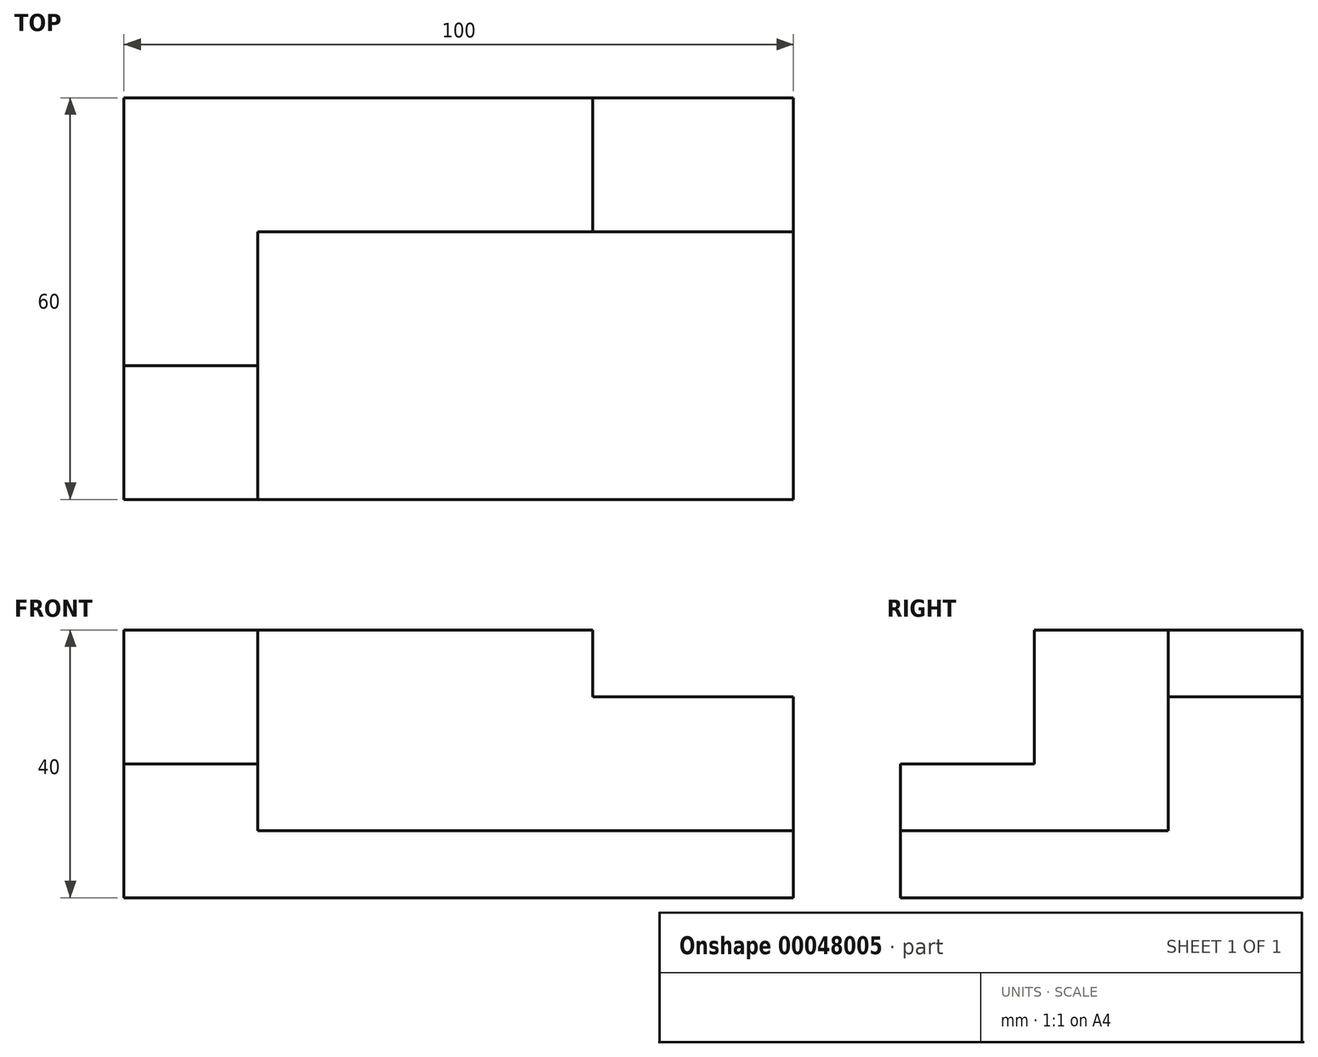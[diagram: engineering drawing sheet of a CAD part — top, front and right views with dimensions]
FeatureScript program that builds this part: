
annotation { "Feature Type Name" : "Feature", "Feature Type Description" : "" }
export const myFeature = defineFeature(function(context is Context, id is Id, definition is map)
    precondition{}
    {
        {
            var Q0;
            Q0=qCreatedBy(makeId("Top.planeOp"),FACE);
            var sketch = newSketch(context, id + "F0", { "sketchPlane" : qUnion([Q0])});
            skLineSegment(sketch, "E0.bottom", {"start": v(0, 0) * mm, "end": v(100, 0) * mm});
            skLineSegment(sketch, "E0.top", {"start": v(0, 60) * mm, "end": v(100, 60) * mm});
            skLineSegment(sketch, "E0.left", {"start": v(0, 0) * mm, "end": v(0, 60) * mm});
            skLineSegment(sketch, "E0.right", {"start": v(100, 0) * mm, "end": v(100, 60) * mm});
            skSolve(sketch);
        }
        {
            var Q0;
            Q0 = qSketchRegion(id + "F0", true);
            extrude(context, id + "F1", {"entities" : qUnion([Q0]), "depth" : 40 * mm});
        }
        {
            var Q0;
            Q0=makeQuery(id+"F1.opExtrude","CAP_FACE",FACE,{"disambiguationData":[OSD([sQuery(id+"F0.wireOp",EDGE,"E0.bottom"),sQuery(id+"F0.wireOp",EDGE,"E0.top"),sQuery(id+"F0.wireOp",EDGE,"E0.left"),sQuery(id+"F0.wireOp",EDGE,"E0.right")])],"isStart":false});
            var sketch = newSketch(context, id + "F2", { "sketchPlane" : qUnion([Q0])});
            skLineSegment(sketch, "E1.bottom", {"start": v(100, 0) * mm, "end": v(20, 0) * mm});
            skLineSegment(sketch, "E1.top", {"start": v(100, 40) * mm, "end": v(20, 40) * mm});
            skLineSegment(sketch, "E1.left", {"start": v(100, 0) * mm, "end": v(100, 40) * mm});
            skLineSegment(sketch, "E1.right", {"start": v(20, 0) * mm, "end": v(20, 40) * mm});
            skSolve(sketch);
        }
        {
            var Q0;
            Q0 = qSketchRegion(id + "F2", true);
            extrude(context, id + "F3", {"entities" : qUnion([Q0]), "operationType" : NewBodyOperationType.REMOVE, "oppositeDirection" : true, "depth" : 30 * mm});
        }
        {
            var Q0;
            Q0=makeQuery(id+"F1.opExtrude","CAP_FACE",FACE,{"disambiguationData":[OSD([sQuery(id+"F0.wireOp",EDGE,"E0.bottom"),sQuery(id+"F0.wireOp",EDGE,"E0.top"),sQuery(id+"F0.wireOp",EDGE,"E0.left"),sQuery(id+"F0.wireOp",EDGE,"E0.right")])],"isStart":false});
            var sketch = newSketch(context, id + "F4", { "sketchPlane" : qUnion([Q0])});
            skLineSegment(sketch, "E2.bottom", {"start": v(0, 0) * mm, "end": v(20, 0) * mm});
            skLineSegment(sketch, "E2.top", {"start": v(0, 20) * mm, "end": v(20, 20) * mm});
            skLineSegment(sketch, "E2.left", {"start": v(0, 0) * mm, "end": v(0, 20) * mm});
            skLineSegment(sketch, "E2.right", {"start": v(20, 0) * mm, "end": v(20, 20) * mm});
            skLineSegment(sketch, "E3.bottom", {"start": v(70, 40) * mm, "end": v(100, 40) * mm});
            skLineSegment(sketch, "E3.top", {"start": v(70, 60) * mm, "end": v(100, 60) * mm});
            skLineSegment(sketch, "E3.left", {"start": v(70, 40) * mm, "end": v(70, 60) * mm});
            skLineSegment(sketch, "E3.right", {"start": v(100, 40) * mm, "end": v(100, 60) * mm});
            skSolve(sketch);
        }
        {
            var Q0;
            Q0=makeQuery(id+"F4.imprint","IMPRINT",FACE,{"disambiguationData":[TD([[makeQuery(id+"F4.imprint","IMPRINT",EDGE,{"derivedFrom":sQuery(id+"F4.wireOp",EDGE,"E3.bottom")}),-1.0]])]});
            extrude(context, id + "F5", {"entities" : qUnion([Q0]), "operationType" : NewBodyOperationType.REMOVE, "oppositeDirection" : true, "depth" : 10 * mm});
        }
        {
            var Q0;
            Q0=makeQuery(id+"F4.imprint","IMPRINT",FACE,{"disambiguationData":[TD([[makeQuery(id+"F4.imprint","IMPRINT",EDGE,{"derivedFrom":sQuery(id+"F4.wireOp",EDGE,"E2.bottom")}),1.0]])]});
            extrude(context, id + "F6", {"entities" : qUnion([Q0]), "operationType" : NewBodyOperationType.REMOVE, "oppositeDirection" : true, "depth" : 20 * mm});
        }
    });
